# Revit family: RN 23102 Valvola diritta
name_source: partatom
category: Rohrzubehör
units: mm (PartAtom-declared; Revit-internal decimal feet)

## family parameters
Arbeitsebenenbasiert = Nein
Beim Laden mit Abzugskörper schneiden = Nein
Bemaßung runder Anschluss = Durchmesser verwenden
Gemeinsam genutzt = Nein
Immer vertikal = Ja
Teiletyp = Ventil - Zerlegung in

## types (4) — shared parameters
1.010.00.2 Blattnummer der Richtlinie = 17
1.010.00.3 Ausgabedatum (Monat) der Richtlinie = 201601
1.010.00.4 Herstellername = R. Nussbaum AG
1.010.00.5 Revisionsdatum der Datei = 20190528
1.010.00.6 Webadresse des Herstellers = http://www.nussbaum.ch
1.100.00.3 Sortiernummer für Anzeigereihenfolge = 1
1.100.00.4 Produktbezeichnung = Absperrarmaturen
1.960/3L.00.8 Link (URL) = https://www.nussbaum.ch
17.700.00.4 Armaturentyp = 1
17.700.00.7 Maximale Betriebstemperatur TB [°C] = 90
17.700.00.8 Maximaler Betriebsdruck (Arbeitsdruck) ps [1.0 · 105 Pa] = 16
Connector Visibility = Nein
EnclosingSpace Visibility = Nein
Hersteller = R. Nussbauzm AG
URL = https://www.nussbaum.ch

## per-type parameters (varying)
| type | 1.800.00.3 TGA-Nummer | 1.810.00.3 Hersteller-Bestellnummer | 1.810.00.4 DATANORM-Nummer | 1.810.00.5 StLB-Nummer | 1.810.00.6 GTIN-Nummer | 17.700.00.30 Produktbeschreibung | 17.700.00.5 Nennweite DN | 17.700.00.6 kvs-Wert [m3/h] | CONNECTOR0_DIAMETER_dX_0r | CONNECTOR0_dX_00 | CONNECTOR0_dX_01 | CONNECTOR0_ref_dX | CONNECTOR1_DIAMETER_dX_0r | CONNECTOR1_dX_00 | CONNECTOR1_dX_01 | CONNECTOR1_ref_dX | Modell | R. Nussbaum AG 23102.04 de Visibility | R. Nussbaum AG 23102.05 de Visibility | R. Nussbaum AG 23102.06 de Visibility | R. Nussbaum AG 23102.07 de Visibility | Typenkommentare |
| DN 15 | 001061???0000000000000000000020070000000000000000100000000 | 23102.04 | 23102.04 | 623.133 | 7612945731906 | 23102.04, Geradsitzventil, mit Entleerventil, DN=15, Rp=½ | 15 | 3.61 | 15 mm  [stored 0.0492126 ft] | 30 mm | 17 mm | 17 mm | 15 mm  [stored 0.0492126 ft] | 17 mm | 30 mm | 17 mm | 23102.04 | Ja | Nein | Nein | Nein | Valvola dirittaDN 15 |
| DN 20 | 001061???0000000000000000000020070000000000000000200000000 | 23102.05 | 23102.05 | 623.134 | 7612945731913 | 23102.05, Geradsitzventil, mit Entleerventil, DN=20, Rp=¾ | 20 | 5.86 | 20 mm | 38 mm | 23 mm | 23 mm | 20 mm | 23 mm | 38 mm | 23 mm | 23102.05 | Nein | Ja | Nein | Nein | Valvola dirittaDN 20 |
| DN 25 | 001061???0000000000000000000020070000000000000000300000000 | 23102.06 | 23102.06 | 623.135 | 7612945728654 | 23102.06, Geradsitzventil, mit Entleerventil, DN=25, Rp=1 | 25 | 9.41 | 25 mm  [stored 0.082021 ft] | 45 mm | 28 mm | 28 mm | 25 mm  [stored 0.082021 ft] | 28 mm | 45 mm | 28 mm | 23102.06 | Nein | Nein | Ja | Nein | Valvola dirittaDN 25 |
| DN 32 | 001061???0000000000000000000020070000000000000000400000000 | 23102.07 | 23102.07 | 623.136 | 7612945728661 | 23102.07, Geradsitzventil, mit Entleerventil, DN=32, Rp=1¼ | 32 | 16.13 | 32 mm | 53 mm | 34 mm | 34 mm | 32 mm | 34 mm | 53 mm | 34 mm | 23102.07 | Nein | Nein | Nein | Ja | Valvola dirittaDN 32 |

note: [stored X ft] marks values corroborated as IEEE doubles in the binary element streams (Revit-internal decimal feet)
